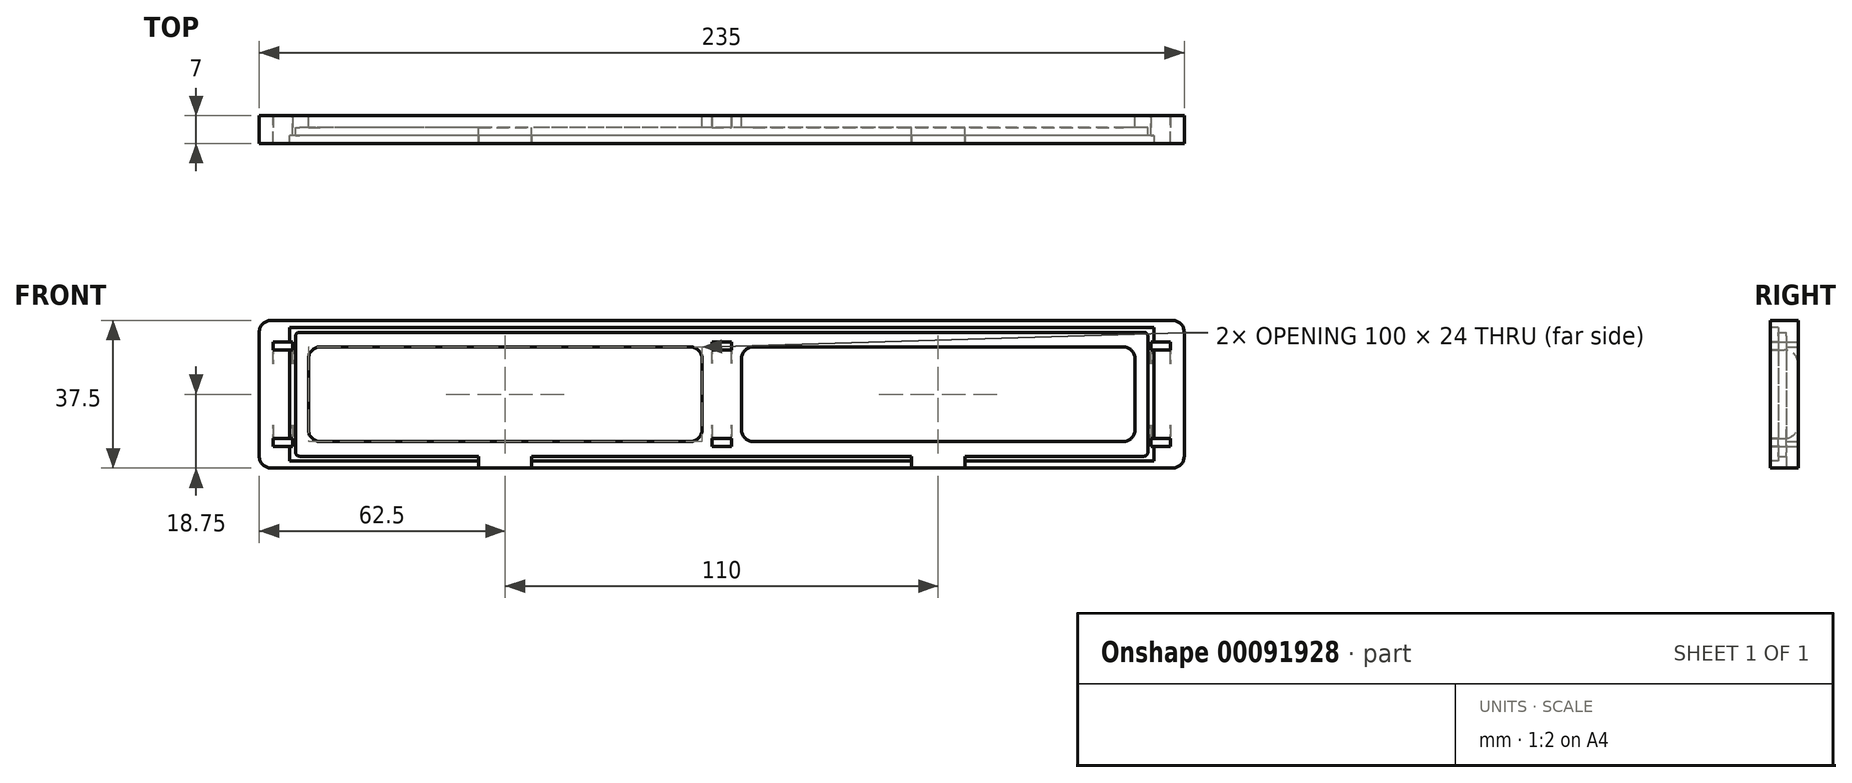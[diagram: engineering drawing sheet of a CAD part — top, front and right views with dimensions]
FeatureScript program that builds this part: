
annotation { "Feature Type Name" : "Feature", "Feature Type Description" : "" }
export const myFeature = defineFeature(function(context is Context, id is Id, definition is map)
    precondition{}
    {
        {
            var Q0;
            Q0=qCreatedBy(makeId("Front.planeOp"),FACE);
            var sketch = newSketch(context, id + "F0", { "sketchPlane" : qUnion([Q0])});
            skLineSegment(sketch, "E0.bottom", {"start": v(114.5, 18.75) * mm, "end": v(-114.5, 18.75) * mm});
            skLineSegment(sketch, "E0.top", {"start": v(114.5, -18.75) * mm, "end": v(-114.5, -18.75) * mm});
            skLineSegment(sketch, "E0.left", {"start": v(117.5, 15.75) * mm, "end": v(117.5, -15.75) * mm});
            skLineSegment(sketch, "E0.right", {"start": v(-117.5, 15.75) * mm, "end": v(-117.5, -15.75) * mm});
            skPoint(sketch, "E0.middle", {"position": v(0, 0) * mm});
            skLineSegment(sketch, "E1.bottom", {"start": v(-8, 12) * mm, "end": v(-102, 12) * mm});
            skLineSegment(sketch, "E1.top", {"start": v(-8, -12) * mm, "end": v(-102, -12) * mm});
            skLineSegment(sketch, "E1.left", {"start": v(-5, 9) * mm, "end": v(-5, -9) * mm});
            skLineSegment(sketch, "E1.right", {"start": v(-105, 9) * mm, "end": v(-105, -9) * mm});
            skPoint(sketch, "E1.middle", {"position": v(-55, 0) * mm});
            skPoint(sketch, "E2.visualSharp", {"position": v(-105, 12) * mm});
            skArc(sketch, "E2.filletArc", {"start": v(-102, 12) * mm, "mid": v(-104.12, 11.12) * mm, "end": v(-105, 9) * mm});
            skPoint(sketch, "E3.visualSharp", {"position": v(-5, 12) * mm});
            skArc(sketch, "E3.filletArc", {"start": v(-5, 9) * mm, "mid": v(-5.88, 11.12) * mm, "end": v(-8, 12) * mm});
            skPoint(sketch, "E4.visualSharp", {"position": v(-5, -12) * mm});
            skArc(sketch, "E4.filletArc", {"start": v(-8, -12) * mm, "mid": v(-5.88, -11.12) * mm, "end": v(-5, -9) * mm});
            skPoint(sketch, "E5.visualSharp", {"position": v(-105, -12) * mm});
            skArc(sketch, "E5.filletArc", {"start": v(-105, -9) * mm, "mid": v(-104.12, -11.12) * mm, "end": v(-102, -12) * mm});
            skArc(sketch, "E6.MirrorCS", {"start": v(102, 12) * mm, "mid": v(104.12, 11.12) * mm, "end": v(105, 9) * mm});
            skArc(sketch, "E7.MirrorCS", {"start": v(5, 9) * mm, "mid": v(5.88, 11.12) * mm, "end": v(8, 12) * mm});
            skArc(sketch, "E8.MirrorCS", {"start": v(8, -12) * mm, "mid": v(5.88, -11.12) * mm, "end": v(5, -9) * mm});
            skArc(sketch, "E9.MirrorCS", {"start": v(105, -9) * mm, "mid": v(104.12, -11.12) * mm, "end": v(102, -12) * mm});
            skLineSegment(sketch, "E10.MirrorCS", {"start": v(8, -12) * mm, "end": v(102, -12) * mm});
            skPoint(sketch, "E11.MirrorP", {"position": v(105, -12) * mm});
            skLineSegment(sketch, "E12.MirrorCS", {"start": v(5, 9) * mm, "end": v(5, -9) * mm});
            skLineSegment(sketch, "E13.MirrorCS", {"start": v(8, 12) * mm, "end": v(102, 12) * mm});
            skLineSegment(sketch, "E14.MirrorCS", {"start": v(105, 9) * mm, "end": v(105, -9) * mm});
            skPoint(sketch, "E15.MirrorP", {"position": v(5, 12) * mm});
            skPoint(sketch, "E16.MirrorP", {"position": v(105, 12) * mm});
            skPoint(sketch, "E17.MirrorP", {"position": v(55, 0) * mm});
            skPoint(sketch, "E18.MirrorP", {"position": v(5, -12) * mm});
            skLineSegment(sketch, "E19.bottom", {"start": v(-2.5, 13.25) * mm, "end": v(2.5, 13.25) * mm});
            skLineSegment(sketch, "E19.top", {"start": v(-2.5, 11.25) * mm, "end": v(2.5, 11.25) * mm});
            skLineSegment(sketch, "E19.left", {"start": v(-2.5, 13.25) * mm, "end": v(-2.5, 11.25) * mm});
            skLineSegment(sketch, "E19.right", {"start": v(2.5, 13.25) * mm, "end": v(2.5, 11.25) * mm});
            skPoint(sketch, "E19.middle", {"position": v(0, 12.25) * mm});
            skLineSegment(sketch, "E20.MirrorCS", {"start": v(2.5, -13.25) * mm, "end": v(2.5, -11.25) * mm});
            skLineSegment(sketch, "E21.MirrorCS", {"start": v(-2.5, -13.25) * mm, "end": v(2.5, -13.25) * mm});
            skLineSegment(sketch, "E22.MirrorCS", {"start": v(-2.5, -11.25) * mm, "end": v(2.5, -11.25) * mm});
            skLineSegment(sketch, "E23.MirrorCS", {"start": v(-2.5, -13.25) * mm, "end": v(-2.5, -11.25) * mm});
            skPoint(sketch, "E24.MirrorP", {"position": v(0, -12.25) * mm});
            skPoint(sketch, "E25.visualSharp", {"position": v(-117.5, 18.75) * mm});
            skArc(sketch, "E25.filletArc", {"start": v(-114.5, 18.75) * mm, "mid": v(-116.62, 17.87) * mm, "end": v(-117.5, 15.75) * mm});
            skPoint(sketch, "E26.visualSharp", {"position": v(-117.5, -18.75) * mm});
            skArc(sketch, "E26.filletArc", {"start": v(-117.5, -15.75) * mm, "mid": v(-116.62, -17.87) * mm, "end": v(-114.5, -18.75) * mm});
            skPoint(sketch, "E27.visualSharp", {"position": v(117.5, -18.75) * mm});
            skArc(sketch, "E27.filletArc", {"start": v(114.5, -18.75) * mm, "mid": v(116.62, -17.87) * mm, "end": v(117.5, -15.75) * mm});
            skPoint(sketch, "E28.visualSharp", {"position": v(117.5, 18.75) * mm});
            skArc(sketch, "E28.filletArc", {"start": v(117.5, 15.75) * mm, "mid": v(116.62, 17.87) * mm, "end": v(114.5, 18.75) * mm});
            skLineSegment(sketch, "E29.bottom", {"start": v(-109, 13.25) * mm, "end": v(-114, 13.25) * mm});
            skLineSegment(sketch, "E29.top", {"start": v(-109, 11.25) * mm, "end": v(-114, 11.25) * mm});
            skLineSegment(sketch, "E29.left", {"start": v(-109, 13.25) * mm, "end": v(-109, 11.25) * mm});
            skLineSegment(sketch, "E29.right", {"start": v(-114, 13.25) * mm, "end": v(-114, 11.25) * mm});
            skPoint(sketch, "E29.middle", {"position": v(-111.5, 12.25) * mm});
            skPoint(sketch, "E29.middle.positionSnap0", {"position": v(-2.5, 12.25) * mm});
            skPoint(sketch, "E29.centerSnap0", {"position": v(-2.5, 12.25) * mm});
            skPoint(sketch, "E30.MirrorP", {"position": v(-111.5, -12.25) * mm});
            skLineSegment(sketch, "E31.MirrorCS", {"start": v(-109, -11.25) * mm, "end": v(-114, -11.25) * mm});
            skLineSegment(sketch, "E32.MirrorCS", {"start": v(-109, -13.25) * mm, "end": v(-109, -11.25) * mm});
            skLineSegment(sketch, "E33.MirrorCS", {"start": v(-109, -13.25) * mm, "end": v(-114, -13.25) * mm});
            skLineSegment(sketch, "E34.MirrorCS", {"start": v(-114, -13.25) * mm, "end": v(-114, -11.25) * mm});
            skLineSegment(sketch, "E35.MirrorCS", {"start": v(114, -13.25) * mm, "end": v(114, -11.25) * mm});
            skLineSegment(sketch, "E36.MirrorCS", {"start": v(109, -13.25) * mm, "end": v(109, -11.25) * mm});
            skLineSegment(sketch, "E37.MirrorCS", {"start": v(114, 13.25) * mm, "end": v(114, 11.25) * mm});
            skLineSegment(sketch, "E38.MirrorCS", {"start": v(109, 13.25) * mm, "end": v(109, 11.25) * mm});
            skLineSegment(sketch, "E39.MirrorCS", {"start": v(109, -11.25) * mm, "end": v(114, -11.25) * mm});
            skLineSegment(sketch, "E40.MirrorCS", {"start": v(109, 13.25) * mm, "end": v(114, 13.25) * mm});
            skLineSegment(sketch, "E41.MirrorCS", {"start": v(109, 11.25) * mm, "end": v(114, 11.25) * mm});
            skLineSegment(sketch, "E42.MirrorCS", {"start": v(109, -13.25) * mm, "end": v(114, -13.25) * mm});
            skPoint(sketch, "E43.MirrorP", {"position": v(111.5, 12.25) * mm});
            skPoint(sketch, "E44.MirrorP", {"position": v(111.5, -12.25) * mm});
            skSolve(sketch);
        }
        {
            var Q0;
            Q0=qSketchRegion(id+"F0",true);
            extrude(context, id + "F1", {"entities" : qUnion([Q0]), "depth" : 3 * mm});
        }
        {
            var Q0;
            Q0=makeQuery(id+"F1.opExtrude","CAP_FACE",FACE,{"disambiguationData":[OSD([sQuery(id+"F0.wireOp",EDGE,"E0.bottom"),sQuery(id+"F0.wireOp",EDGE,"E0.top"),sQuery(id+"F0.wireOp",EDGE,"E0.left"),sQuery(id+"F0.wireOp",EDGE,"E0.right"),sQuery(id+"F0.wireOp",EDGE,"E1.bottom"),sQuery(id+"F0.wireOp",EDGE,"E1.top"),sQuery(id+"F0.wireOp",EDGE,"E1.left"),sQuery(id+"F0.wireOp",EDGE,"E1.right"),sQuery(id+"F0.wireOp",EDGE,"E2.filletArc"),sQuery(id+"F0.wireOp",EDGE,"E3.filletArc"),sQuery(id+"F0.wireOp",EDGE,"E4.filletArc"),sQuery(id+"F0.wireOp",EDGE,"E5.filletArc"),sQuery(id+"F0.wireOp",EDGE,"E6.MirrorCS"),sQuery(id+"F0.wireOp",EDGE,"E7.MirrorCS"),sQuery(id+"F0.wireOp",EDGE,"E8.MirrorCS"),sQuery(id+"F0.wireOp",EDGE,"E9.MirrorCS"),sQuery(id+"F0.wireOp",EDGE,"E10.MirrorCS"),sQuery(id+"F0.wireOp",EDGE,"E12.MirrorCS"),sQuery(id+"F0.wireOp",EDGE,"E13.MirrorCS"),sQuery(id+"F0.wireOp",EDGE,"E14.MirrorCS")])],"isStart":false});
            var sketch = newSketch(context, id + "F2", { "sketchPlane" : qUnion([Q0])});
            skLineSegment(sketch, "E45.bottom", {"start": v(107.25, 15.75) * mm, "end": v(-107.25, 15.75) * mm});
            skLineSegment(sketch, "E45.top", {"start": v(107.25, -15.75) * mm, "end": v(-107.25, -15.75) * mm});
            skLineSegment(sketch, "E45.left", {"start": v(108.25, 14.75) * mm, "end": v(108.25, -14.75) * mm});
            skLineSegment(sketch, "E45.right", {"start": v(-108.25, 14.75) * mm, "end": v(-108.25, -14.75) * mm});
            skPoint(sketch, "E46.visualSharp", {"position": v(-108.25, 15.75) * mm});
            skArc(sketch, "E46.filletArc", {"start": v(-107.25, 15.75) * mm, "mid": v(-107.96, 15.46) * mm, "end": v(-108.25, 14.75) * mm});
            skPoint(sketch, "E47.visualSharp", {"position": v(108.25, 15.75) * mm});
            skArc(sketch, "E47.filletArc", {"start": v(108.25, 14.75) * mm, "mid": v(107.96, 15.46) * mm, "end": v(107.25, 15.75) * mm});
            skPoint(sketch, "E48.visualSharp", {"position": v(108.25, -15.75) * mm});
            skArc(sketch, "E48.filletArc", {"start": v(107.25, -15.75) * mm, "mid": v(107.96, -15.46) * mm, "end": v(108.25, -14.75) * mm});
            skPoint(sketch, "E49.visualSharp", {"position": v(-108.25, -15.75) * mm});
            skArc(sketch, "E49.filletArc", {"start": v(-108.25, -14.75) * mm, "mid": v(-107.96, -15.46) * mm, "end": v(-107.25, -15.75) * mm});
            skSolve(sketch);
        }
        {
            var Q0;
            Q0=makeQuery(id+"F2.imprint","IMPRINT",FACE,{"disambiguationData":[TD([[makeQuery(id+"F2.imprint","IMPRINT",EDGE,{"derivedFrom":sQuery(id+"F2.wireOp",EDGE,"E45.bottom")}),-1.0]])]});
            var Q1;
            Q1=makeQuery(id+"F2.imprint","IMPRINT",FACE,{"disambiguationData":[TD([[makeQuery(id+"F2.imprint","IMPRINT",EDGE,{"derivedFrom":sQuery(id+"F2.wireOp",EDGE,"8UQ35Aj4-GzFw-aaHB-QqC8-tIVl76PQ1ExV")}),1.0]])]});
            extrude(context, id + "F3", {"entities" : qUnion([Q0, Q1]), "operationType" : NewBodyOperationType.ADD, "depth" : 4 * mm});
        }
        {
            var Q0;
            Q0=makeQuery(id+"F3.opExtrude","CAP_FACE",FACE,{"disambiguationData":[OSD([sQuery(id+"F0.wireOp",EDGE,"E0.bottom"),sQuery(id+"F0.wireOp",EDGE,"E0.top"),sQuery(id+"F0.wireOp",EDGE,"E0.left"),sQuery(id+"F0.wireOp",EDGE,"E0.right"),sQuery(id+"F0.wireOp",EDGE,"ZHHTkMPx-xk2V-YnWK-Tyof-4nBsazcNe8Yu"),sQuery(id+"F0.wireOp",EDGE,"0744b17f-897b-458e-b34b-7ca158b34d090.MirrorCS"),sQuery(id+"F2.wireOp",EDGE,"E45.bottom"),sQuery(id+"F2.wireOp",EDGE,"E45.top"),sQuery(id+"F2.wireOp",EDGE,"E45.left"),sQuery(id+"F2.wireOp",EDGE,"E45.right"),sQuery(id+"F2.wireOp",EDGE,"E46.filletArc"),sQuery(id+"F2.wireOp",EDGE,"E47.filletArc"),sQuery(id+"F2.wireOp",EDGE,"E48.filletArc"),sQuery(id+"F2.wireOp",EDGE,"E49.filletArc"),sQuery(id+"F2.wireOp",EDGE,"21LFbrld-Wxhg-M3QD-jiVL-tybxt2T7NddJ"),sQuery(id+"F2.wireOp",EDGE,"745e8d08-7811-4726-80f7-b7a76f0ceae30.MirrorC")])],"isStart":false});
            var sketch = newSketch(context, id + "F4", { "sketchPlane" : qUnion([Q0])});
            skLineSegment(sketch, "E50.bottom", {"start": v(109.75, 17) * mm, "end": v(-109.75, 17) * mm});
            skLineSegment(sketch, "E50.top", {"start": v(109.75, -17) * mm, "end": v(-109.75, -17) * mm});
            skLineSegment(sketch, "E50.left", {"start": v(109.75, 17) * mm, "end": v(109.75, -17) * mm});
            skLineSegment(sketch, "E50.right", {"start": v(-109.75, 17) * mm, "end": v(-109.75, -17) * mm});
            skPoint(sketch, "E50.middle", {"position": v(0, 0) * mm});
            skLineSegment(sketch, "E51.bottom", {"start": v(107.27, 14.5) * mm, "end": v(-107.27, 14.5) * mm});
            skLineSegment(sketch, "E51.top", {"start": v(107.27, -14.5) * mm, "end": v(-107.27, -14.5) * mm});
            skLineSegment(sketch, "E51.left", {"start": v(107.27, 14.5) * mm, "end": v(107.27, -14.5) * mm});
            skLineSegment(sketch, "E51.right", {"start": v(-107.27, 14.5) * mm, "end": v(-107.27, -14.5) * mm});
            skSolve(sketch);
        }
        {
            var Q0;
            Q0=qSketchRegion(id+"F4",true);
            extrude(context, id + "F5", {"entities" : qUnion([Q0]), "operationType" : NewBodyOperationType.REMOVE, "oppositeDirection" : true, "depth" : 2 * mm});
        }
        {
            var Q0;
            {var subQ0=sQuery(id+"F0.wireOp",EDGE,"E0.top");Q0=makeQuery(id+"F3.boolean.opBoolean","MERGE",FACE,{"derivedFrom":[makeQuery(id+"F1.opExtrude","SWEPT_FACE",FACE,{"disambiguationData":[OSD([subQ0])]}),makeQuery(id+"F3.opExtrude","SWEPT_FACE",FACE,{"disambiguationData":[OSD([subQ0])]})]});}
            var sketch = newSketch(context, id + "F6", { "sketchPlane" : qUnion([Q0])});
            skLineSegment(sketch, "E52.bottom", {"start": v(-61.75, 7) * mm, "end": v(-48.25, 7) * mm});
            skLineSegment(sketch, "E52.top", {"start": v(-61.75, 3) * mm, "end": v(-48.25, 3) * mm});
            skLineSegment(sketch, "E52.left", {"start": v(-61.75, 7) * mm, "end": v(-61.75, 3) * mm});
            skLineSegment(sketch, "E52.right", {"start": v(-48.25, 7) * mm, "end": v(-48.25, 3) * mm});
            skPoint(sketch, "E53", {"position": v(-55, 3) * mm});
            skPoint(sketch, "E54.MirrorP", {"position": v(55, 3) * mm});
            skLineSegment(sketch, "E55.MirrorCS", {"start": v(61.75, 7) * mm, "end": v(48.25, 7) * mm});
            skLineSegment(sketch, "E56.MirrorCS", {"start": v(61.75, 3) * mm, "end": v(48.25, 3) * mm});
            skLineSegment(sketch, "E57.MirrorCS", {"start": v(48.25, 7) * mm, "end": v(48.25, 3) * mm});
            skLineSegment(sketch, "E58.MirrorCS", {"start": v(61.75, 7) * mm, "end": v(61.75, 3) * mm});
            skSolve(sketch);
        }
        {
            var Q0;
            Q0=qSketchRegion(id+"F6",true);
            extrude(context, id + "F7", {"entities" : qUnion([Q0]), "operationType" : NewBodyOperationType.REMOVE, "oppositeDirection" : true, "depth" : 25 * mm});
        }
        {
            var Q0;
            Q0=makeQuery(id+"F1.opExtrude","CAP_EDGE",EDGE,{"disambiguationData":[OSD([sQuery(id+"F0.wireOp",EDGE,"E19.top")])],"isStart":true});
            var Q1;
            Q1=makeQuery(id+"F1.opExtrude","CAP_EDGE",EDGE,{"disambiguationData":[OSD([sQuery(id+"F0.wireOp",EDGE,"E22.MirrorCS")])],"isStart":true});
            var Q2;
            Q2=makeQuery(id+"F1.opExtrude","CAP_EDGE",EDGE,{"disambiguationData":[OSD([sQuery(id+"F0.wireOp",EDGE,"E41.MirrorCS")])],"isStart":true});
            var Q3;
            Q3=makeQuery(id+"F1.opExtrude","CAP_EDGE",EDGE,{"disambiguationData":[OSD([sQuery(id+"F0.wireOp",EDGE,"E39.MirrorCS")])],"isStart":true});
            var Q4;
            Q4=makeQuery(id+"F1.opExtrude","CAP_EDGE",EDGE,{"disambiguationData":[OSD([sQuery(id+"F0.wireOp",EDGE,"E31.MirrorCS")])],"isStart":true});
            var Q5;
            Q5=makeQuery(id+"F1.opExtrude","CAP_EDGE",EDGE,{"disambiguationData":[OSD([sQuery(id+"F0.wireOp",EDGE,"E29.top")])],"isStart":true});
            fillet(context, id + "F8", {"entities" : qUnion([Q0, Q1, Q2, Q3, Q4, Q5]), "radius" : 3.5 * mm, "tangentPropagation" : true, "allowEdgeOverflow" : false});
        }
    });
